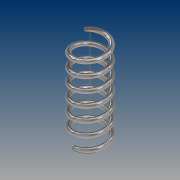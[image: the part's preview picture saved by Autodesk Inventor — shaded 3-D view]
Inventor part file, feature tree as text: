
AUTODESK INVENTOR PART (.ipt)
format: ipt  version: 2021 (Build 250183000, 183)  size: 271,872 bytes
history: native  units: mm
features: sketch x2, extrude x1, helix x1
ambient origin geometry x8: Origin, YZ Plane, XZ Plane, XY Plane, X Axis, Y Axis, Z Axis, Center Point
bodies: Solid1 (feature_tree)
feature tree (4):
  extrude  "Extrusion1"  Depth=3.6mm
  helix  "Coil1"  [1 undecoded]
  sketch  "Sketch1"  dims[d0=1.0mm d1=3.6mm d2=20.0mm d3=0.0mm]
  sketch  "Sketch2"  dims[d4=3.0mm d5=20.0mm d6=10.0mm d7=0.0mm d8=90.0deg d9=90.0deg d10=0.0mm d11=0.0mm]
note: 1 required parameter value undecoded (feature->parameter linkage not recoverable at this tier; creation-order binding heuristic only, values carry confidence <= 0.55)
